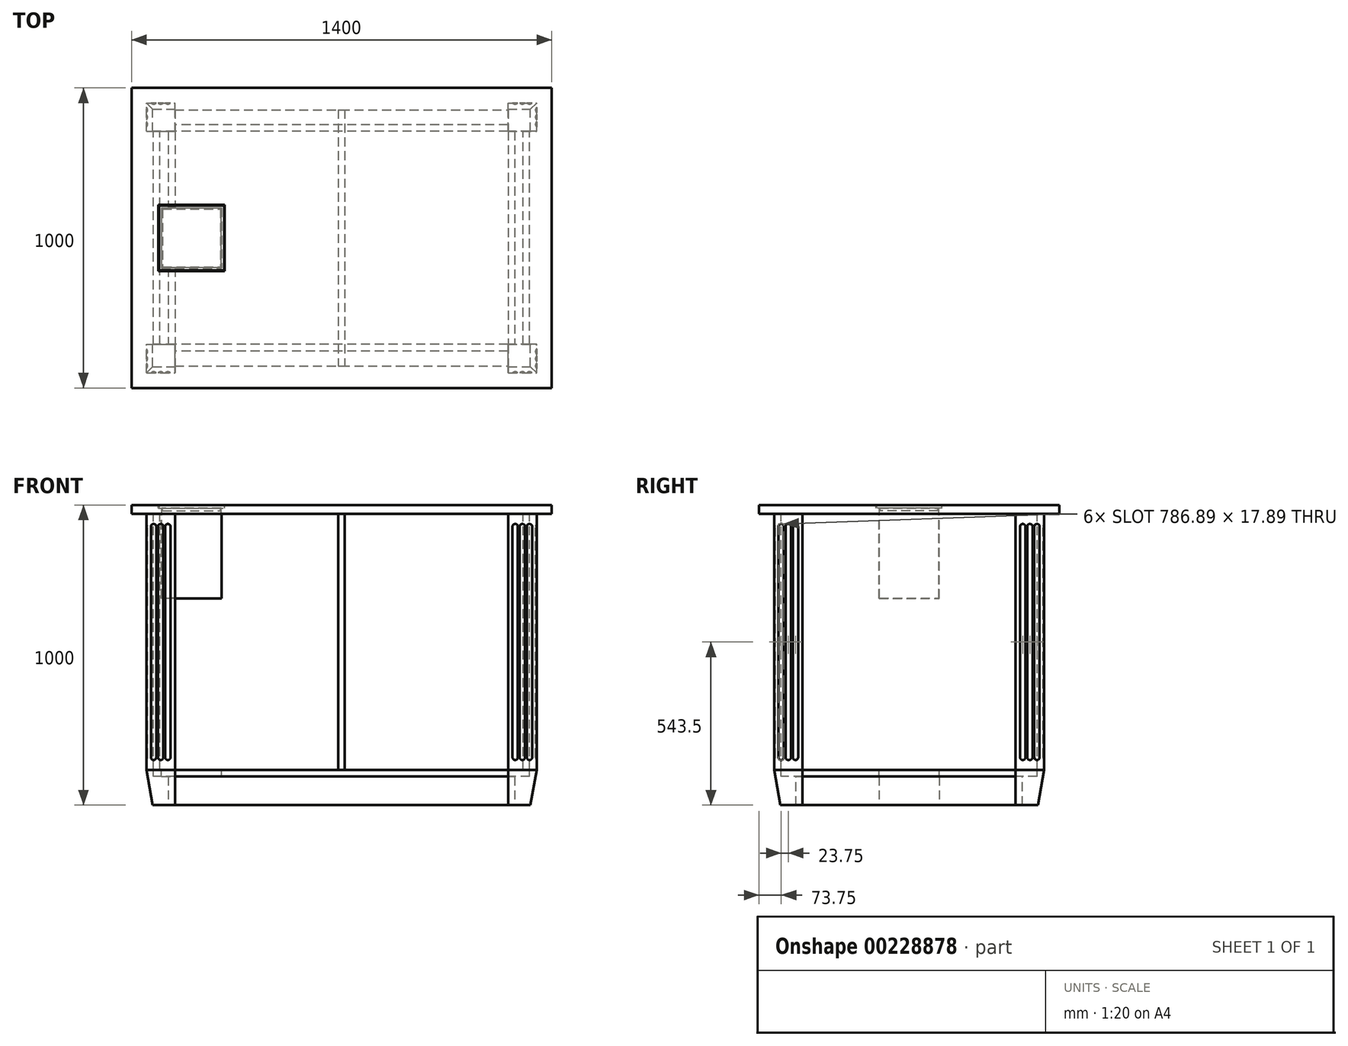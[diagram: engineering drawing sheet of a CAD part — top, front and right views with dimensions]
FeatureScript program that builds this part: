
annotation { "Feature Type Name" : "Feature", "Feature Type Description" : "" }
export const myFeature = defineFeature(function(context is Context, id is Id, definition is map)
    precondition{}
    {
        {
            assignVariable(context, id + "F0", {"name" : "Height", "anyValue" : 1000});
        }
        {
            assignVariable(context, id + "F1", {"name" : "TopThickness", "anyValue" : 30});
        }
        {
            var Q0;
            Q0=qCreatedBy(makeId("Top.planeOp"),FACE);
            cPlane(context, id + "F2", {"entities" : qUnion([Q0]), "cplaneType" : CPlaneType.OFFSET, "offset" : (getVariable(context, 'Height')) * mm, "width" : 150 * mm, "height" : 150 * mm});
        }
        {
            var Q0;
            Q0=qCreatedBy(id+"F2.planeOp",FACE);
            var sketch = newSketch(context, id + "F3", { "sketchPlane" : qUnion([Q0])});
            skLineSegment(sketch, "E0.bottom", {"start": v(700, -500) * mm, "end": v(-700, -500) * mm});
            skLineSegment(sketch, "E0.top", {"start": v(700, 500) * mm, "end": v(-700, 500) * mm});
            skLineSegment(sketch, "E0.left", {"start": v(700, -500) * mm, "end": v(700, 500) * mm});
            skLineSegment(sketch, "E0.right", {"start": v(-700, -500) * mm, "end": v(-700, 500) * mm});
            skPoint(sketch, "E0.middle", {"position": v(0, 0) * mm});
            skSolve(sketch);
        }
        {
            var Q0;
            Q0 = qSketchRegion(id + "F3", true);
            extrude(context, id + "F4", {"entities" : qUnion([Q0]), "oppositeDirection" : true, "depth" : (getVariable(context, 'TopThickness')) * mm});
        }
        {
            var Q0;
            Q0=qCreatedBy(makeId("Top.planeOp"),FACE);
            var sketch = newSketch(context, id + "F5", { "sketchPlane" : qUnion([Q0])});
            skLineSegment(sketch, "E1.bottom", {"start": v(-650, -450) * mm, "end": v(-555, -450) * mm});
            skLineSegment(sketch, "E1.top", {"start": v(-650, -355) * mm, "end": v(-555, -355) * mm});
            skLineSegment(sketch, "E1.left", {"start": v(-650, -450) * mm, "end": v(-650, -355) * mm});
            skLineSegment(sketch, "E1.right", {"start": v(-555, -450) * mm, "end": v(-555, -355) * mm});
            skLineSegment(sketch, "E2.bottom", {"start": v(555, -450) * mm, "end": v(650, -450) * mm});
            skLineSegment(sketch, "E2.top", {"start": v(555, -355) * mm, "end": v(650, -355) * mm});
            skLineSegment(sketch, "E2.left", {"start": v(555, -450) * mm, "end": v(555, -355) * mm});
            skLineSegment(sketch, "E2.right", {"start": v(650, -450) * mm, "end": v(650, -355) * mm});
            skLineSegment(sketch, "E3.bottom", {"start": v(-650, 355) * mm, "end": v(-555, 355) * mm});
            skLineSegment(sketch, "E3.top", {"start": v(-650, 450) * mm, "end": v(-555, 450) * mm});
            skLineSegment(sketch, "E3.left", {"start": v(-650, 355) * mm, "end": v(-650, 450) * mm});
            skLineSegment(sketch, "E3.right", {"start": v(-555, 355) * mm, "end": v(-555, 450) * mm});
            skLineSegment(sketch, "E4.bottom", {"start": v(555, 355) * mm, "end": v(650, 355) * mm});
            skLineSegment(sketch, "E4.top", {"start": v(555, 450) * mm, "end": v(650, 450) * mm});
            skLineSegment(sketch, "E4.left", {"start": v(555, 355) * mm, "end": v(555, 450) * mm});
            skLineSegment(sketch, "E4.right", {"start": v(650, 355) * mm, "end": v(650, 450) * mm});
            skSolve(sketch);
        }
        {
            var Q0;
            Q0 = qSketchRegion(id + "F5", true);
            var Q1;
            Q1=makeQuery(id+"F4.opExtrude","CAP_FACE",FACE,{"disambiguationData":[OSD([sQuery(id+"F3.wireOp",EDGE,"E0.bottom"),sQuery(id+"F3.wireOp",EDGE,"E0.top"),sQuery(id+"F3.wireOp",EDGE,"E0.left"),sQuery(id+"F3.wireOp",EDGE,"E0.right")])],"isStart":false});
            extrude(context, id + "F6", {"entities" : qUnion([Q0]), "endBound" : BoundingType.UP_TO_SURFACE, "endBoundEntityFace" : qUnion([Q1]), "depth" : 25 * mm});
        }
        {
            var Q0;
            Q0=makeQuery(id+"F6.opExtrude","SWEPT_FACE",FACE,{"disambiguationData":[OSD([sQuery(id+"F5.wireOp",EDGE,"E1.right")])]});
            var sketch = newSketch(context, id + "F7", { "sketchPlane" : qUnion([Q0])});
            skLineSegment(sketch, "E5.bottom", {"start": v(-355, 95) * mm, "end": v(-377, 95) * mm});
            skLineSegment(sketch, "E5.top", {"start": v(-355, 0) * mm, "end": v(-377, 0) * mm});
            skLineSegment(sketch, "E5.left", {"start": v(-355, 95) * mm, "end": v(-355, 0) * mm});
            skLineSegment(sketch, "E5.right", {"start": v(-377, 95) * mm, "end": v(-377, 0) * mm});
            skSolve(sketch);
        }
        {
            var Q0;
            Q0 = qSketchRegion(id + "F7", true);
            var Q1;
            Q1=makeQuery(id+"F6.opExtrude","SWEPT_FACE",FACE,{"disambiguationData":[OSD([sQuery(id+"F5.wireOp",EDGE,"E2.left")])]});
            extrude(context, id + "F8", {"entities" : qUnion([Q0]), "endBound" : BoundingType.UP_TO_SURFACE, "endBoundEntityFace" : qUnion([Q1]), "depth" : 25 * mm});
        }
        {
            var Q0;
            Q0=makeQuery(id+"F8.opExtrude","SWEPT_BODY",BODY,{"disambiguationData":[OSD([sQuery(id+"F7.wireOp",EDGE,"E5.bottom"),sQuery(id+"F7.wireOp",EDGE,"E5.top"),sQuery(id+"F7.wireOp",EDGE,"E5.left"),sQuery(id+"F7.wireOp",EDGE,"E5.right")])]});
            var Q1;
            Q1=qCreatedBy(makeId("Front.planeOp"),FACE);
            mirror(context, id + "F9", {"entities" : qUnion([Q0]), "mirrorPlane" : qUnion([Q1])});
        }
        {
            var Q0;
            Q0=makeQuery(id+"F6.opExtrude","SWEPT_FACE",FACE,{"disambiguationData":[OSD([sQuery(id+"F5.wireOp",EDGE,"E2.top")])]});
            var sketch = newSketch(context, id + "F10", { "sketchPlane" : qUnion([Q0])});
            skLineSegment(sketch, "E6.bottom", {"start": v(-555, 95) * mm, "end": v(-577, 95) * mm});
            skLineSegment(sketch, "E6.top", {"start": v(-555, 0) * mm, "end": v(-577, 0) * mm});
            skLineSegment(sketch, "E6.left", {"start": v(-555, 95) * mm, "end": v(-555, 0) * mm});
            skLineSegment(sketch, "E6.right", {"start": v(-577, 95) * mm, "end": v(-577, 0) * mm});
            skSolve(sketch);
        }
        {
            var Q0;
            Q0 = qSketchRegion(id + "F10", true);
            var Q1;
            Q1=makeQuery(id+"F6.opExtrude","SWEPT_FACE",FACE,{"disambiguationData":[OSD([sQuery(id+"F5.wireOp",EDGE,"E4.bottom")])]});
            extrude(context, id + "F11", {"entities" : qUnion([Q0]), "endBound" : BoundingType.UP_TO_SURFACE, "endBoundEntityFace" : qUnion([Q1]), "depth" : 25 * mm});
        }
        {
            var Q0;
            Q0=makeQuery(id+"F11.opExtrude","SWEPT_BODY",BODY,{"disambiguationData":[OSD([sQuery(id+"F10.wireOp",EDGE,"E6.bottom"),sQuery(id+"F10.wireOp",EDGE,"E6.top"),sQuery(id+"F10.wireOp",EDGE,"E6.left"),sQuery(id+"F10.wireOp",EDGE,"E6.right")])]});
            var Q1;
            Q1=qCreatedBy(makeId("Right.planeOp"),FACE);
            mirror(context, id + "F12", {"entities" : qUnion([Q0]), "mirrorPlane" : qUnion([Q1])});
        }
        {
            var Q0;
            Q0=makeQuery(id+"F11.opExtrude","SWEPT_FACE",FACE,{"disambiguationData":[OSD([sQuery(id+"F10.wireOp",EDGE,"E6.bottom")])]});
            var sketch = newSketch(context, id + "F13", { "sketchPlane" : qUnion([Q0])});
            skLineSegment(sketch, "E7.bottom", {"start": v(-627, 427) * mm, "end": v(627, 427) * mm});
            skLineSegment(sketch, "E7.top", {"start": v(-627, -427) * mm, "end": v(627, -427) * mm});
            skLineSegment(sketch, "E7.left", {"start": v(-627, 427) * mm, "end": v(-627, -427) * mm});
            skLineSegment(sketch, "E7.right", {"start": v(627, 427) * mm, "end": v(627, -427) * mm});
            skPoint(sketch, "E7.middle", {"position": v(0, 0) * mm});
            skSolve(sketch);
        }
        {
            var Q0;
            Q0 = qSketchRegion(id + "F13", true);
            extrude(context, id + "F14", {"entities" : qUnion([Q0]), "depth" : 22 * mm});
        }
        {
            var Q0;
            Q0=makeQuery(id+"F6.opExtrude","SWEPT_BODY",BODY,{"disambiguationData":[OSD([sQuery(id+"F5.wireOp",EDGE,"E4.bottom"),sQuery(id+"F5.wireOp",EDGE,"E4.top"),sQuery(id+"F5.wireOp",EDGE,"E4.left"),sQuery(id+"F5.wireOp",EDGE,"E4.right")])]});
            var Q1;
            Q1=makeQuery(id+"F6.opExtrude","SWEPT_BODY",BODY,{"disambiguationData":[OSD([sQuery(id+"F5.wireOp",EDGE,"E2.bottom"),sQuery(id+"F5.wireOp",EDGE,"E2.top"),sQuery(id+"F5.wireOp",EDGE,"E2.left"),sQuery(id+"F5.wireOp",EDGE,"E2.right")])]});
            var Q2;
            Q2=makeQuery(id+"F6.opExtrude","SWEPT_BODY",BODY,{"disambiguationData":[OSD([sQuery(id+"F5.wireOp",EDGE,"E1.bottom"),sQuery(id+"F5.wireOp",EDGE,"E1.top"),sQuery(id+"F5.wireOp",EDGE,"E1.left"),sQuery(id+"F5.wireOp",EDGE,"E1.right")])]});
            var Q3;
            Q3=makeQuery(id+"F6.opExtrude","SWEPT_BODY",BODY,{"disambiguationData":[OSD([sQuery(id+"F5.wireOp",EDGE,"E3.bottom"),sQuery(id+"F5.wireOp",EDGE,"E3.top"),sQuery(id+"F5.wireOp",EDGE,"E3.left"),sQuery(id+"F5.wireOp",EDGE,"E3.right")])]});
            var Q4;
            Q4=makeQuery(id+"F14.opExtrude","SWEPT_BODY",BODY,{"disambiguationData":[OSD([sQuery(id+"F13.wireOp",EDGE,"E7.bottom"),sQuery(id+"F13.wireOp",EDGE,"E7.top"),sQuery(id+"F13.wireOp",EDGE,"E7.left"),sQuery(id+"F13.wireOp",EDGE,"E7.right")])]});
            booleanBodies(context, id + "F15", {"operationType" : BooleanOperationType.SUBTRACTION, "tools" : qUnion([Q0, Q1, Q2, Q3]), "targets" : qUnion([Q4]), "keepTools" : true});
        }
        {
            var Q0;
            Q0=makeQuery(id+"F6.opExtrude","SWEPT_FACE",FACE,{"disambiguationData":[OSD([sQuery(id+"F5.wireOp",EDGE,"E3.bottom")])]});
            var sketch = newSketch(context, id + "F16", { "sketchPlane" : qUnion([Q0])});
            skLineSegment(sketch, "E8.bottom", {"start": v(-627, 970) * mm, "end": v(-605, 970) * mm});
            skLineSegment(sketch, "E8.top", {"start": v(-627, 117) * mm, "end": v(-605, 117) * mm});
            skLineSegment(sketch, "E8.left", {"start": v(-627, 970) * mm, "end": v(-627, 117) * mm});
            skLineSegment(sketch, "E8.right", {"start": v(-605, 970) * mm, "end": v(-605, 117) * mm});
            skSolve(sketch);
        }
        {
            var Q0;
            Q0 = qSketchRegion(id + "F16", true);
            extrude(context, id + "F17", {"entities" : qUnion([Q0]), "endBound" : BoundingType.UP_TO_NEXT, "depth" : 25 * mm});
        }
        {
            var Q0;
            Q0=makeQuery(id+"F17.opExtrude","SWEPT_BODY",BODY,{"disambiguationData":[OSD([sQuery(id+"F16.wireOp",EDGE,"E8.bottom"),sQuery(id+"F16.wireOp",EDGE,"E8.top"),sQuery(id+"F16.wireOp",EDGE,"E8.left"),sQuery(id+"F16.wireOp",EDGE,"E8.right")])]});
            var Q1;
            Q1=qCreatedBy(makeId("Right.planeOp"),FACE);
            mirror(context, id + "F18", {"entities" : qUnion([Q0]), "mirrorPlane" : qUnion([Q1])});
        }
        {
            var Q0;
            Q0=makeQuery(id+"F6.opExtrude","SWEPT_FACE",FACE,{"disambiguationData":[OSD([sQuery(id+"F5.wireOp",EDGE,"E2.right")])]});
            var sketch = newSketch(context, id + "F19", { "sketchPlane" : qUnion([Q0])});
            skLineSegment(sketch, "E9", {"start": v(-450, 117) * mm, "end": v(-424.72, -26.37) * mm});
            skLineSegment(sketch, "E10", {"start": v(-424.72, -26.37) * mm, "end": v(-510.23, -26.37) * mm});
            skLineSegment(sketch, "E11", {"start": v(-510.23, -26.37) * mm, "end": v(-450, 117) * mm});
            skLineSegment(sketch, "E12.0", {"start": v(355, 117) * mm, "end": v(-355, 117) * mm, "construction": true});
            skLineSegment(sketch, "E13", {"start": v(-355, 117) * mm, "end": v(-576.45, 117) * mm, "construction": true});
            skLineSegment(sketch, "E14.0", {"start": v(450, 970) * mm, "end": v(450, 0) * mm, "construction": true});
            skLineSegment(sketch, "E15", {"start": v(355, 117) * mm, "end": v(613.82, 117) * mm, "construction": true});
            skLineSegment(sketch, "E16", {"start": v(450, 117) * mm, "end": v(417.76, -65.85) * mm});
            skLineSegment(sketch, "E17", {"start": v(417.76, -65.85) * mm, "end": v(573.8, -58.45) * mm});
            skLineSegment(sketch, "E18", {"start": v(573.8, -58.45) * mm, "end": v(450, 117) * mm});
            skSolve(sketch);
        }
        {
            var Q0;
            Q0 = qSketchRegion(id + "F19", true);
            extrude(context, id + "F20", {"entities" : qUnion([Q0]), "operationType" : NewBodyOperationType.REMOVE, "endBound" : BoundingType.THROUGH_ALL, "oppositeDirection" : true, "depth" : 25 * mm});
        }
        {
            var Q0;
            Q0=makeQuery(id+"F6.opExtrude","SWEPT_FACE",FACE,{"disambiguationData":[OSD([sQuery(id+"F5.wireOp",EDGE,"E4.top")])]});
            var sketch = newSketch(context, id + "F21", { "sketchPlane" : qUnion([Q0])});
            skLineSegment(sketch, "E19.0", {"start": v(555, 117) * mm, "end": v(-555, 117) * mm, "construction": true});
            skLineSegment(sketch, "E20", {"start": v(-555, 117) * mm, "end": v(-830.8, 117) * mm, "construction": true});
            skLineSegment(sketch, "E21", {"start": v(-650, 117) * mm, "end": v(-621.11, -46.82) * mm});
            skLineSegment(sketch, "E22", {"start": v(-621.11, -46.82) * mm, "end": v(-744.4, -46.82) * mm});
            skLineSegment(sketch, "E23", {"start": v(-744.4, -46.82) * mm, "end": v(-650, 117) * mm});
            skLineSegment(sketch, "E24", {"start": v(650, 117) * mm, "end": v(608.3, -119.45) * mm});
            skLineSegment(sketch, "E25", {"start": v(608.3, -119.45) * mm, "end": v(784.77, -119.45) * mm});
            skLineSegment(sketch, "E26", {"start": v(784.77, -119.45) * mm, "end": v(650, 117) * mm});
            skLineSegment(sketch, "E27.0", {"start": v(650, 970) * mm, "end": v(650, 0) * mm, "construction": true});
            skLineSegment(sketch, "E28", {"start": v(555, 117) * mm, "end": v(857.57, 117) * mm, "construction": true});
            skSolve(sketch);
        }
        {
            var Q0;
            Q0 = qSketchRegion(id + "F21", true);
            extrude(context, id + "F22", {"entities" : qUnion([Q0]), "operationType" : NewBodyOperationType.REMOVE, "endBound" : BoundingType.THROUGH_ALL, "oppositeDirection" : true, "depth" : 25 * mm});
        }
        {
            var Q0;
            Q0=makeQuery(id+"F6.opExtrude","SWEPT_FACE",FACE,{"disambiguationData":[OSD([sQuery(id+"F5.wireOp",EDGE,"E2.top")])]});
            var Q1;
            Q1=makeQuery(id+"F6.opExtrude","SWEPT_FACE",FACE,{"disambiguationData":[OSD([sQuery(id+"F5.wireOp",EDGE,"E2.bottom")])]});
            cPlane(context, id + "F23", {"entities" : qUnion([Q0, Q1]), "cplaneType" : CPlaneType.MID_PLANE, "offset" : 25 * mm, "width" : 150 * mm, "height" : 150 * mm});
        }
        {
            var Q0;
            Q0=qCreatedBy(id+"F23.planeOp",FACE);
            var sketch = newSketch(context, id + "F24", { "sketchPlane" : qUnion([Q0])});
            skLineSegment(sketch, "E29", {"start": v(-658, 940) * mm, "end": v(-658, 147) * mm});
            skLineSegment(sketch, "E30", {"start": v(-646, 928) * mm, "end": v(-646, 159) * mm});
            skLineSegment(sketch, "E31.0", {"start": v(-555, 117) * mm, "end": v(-650, 117) * mm, "construction": true});
            skLineSegment(sketch, "E32.0", {"start": v(-700, 970) * mm, "end": v(700, 970) * mm, "construction": true});
            skArc(sketch, "E33", {"start": v(-646, 159) * mm, "mid": v(-649.51, 150.51) * mm, "end": v(-658, 147) * mm});
            skArc(sketch, "E34", {"start": v(-646, 928) * mm, "mid": v(-649.51, 936.49) * mm, "end": v(-658, 940) * mm});
            skSolve(sketch);
        }
        {
            var Q0;
            Q0 = qSketchRegion(id + "F24", true);
            var Q1;
            Q1=sQuery(id+"F24.wireOp",EDGE,"E29");
            revolve(context, id + "F25", {"entities" : qUnion([Q0]), "axis" : qUnion([Q1]), "revolveType" : RevolveType.FULL});
        }
        {
            var Q0;
            Q0=makeQuery(id+"F25.opRevolve","SWEPT_BODY",BODY,{"disambiguationData":[OSD([sQuery(id+"F24.wireOp",EDGE,"E29"),sQuery(id+"F24.wireOp",EDGE,"E30"),sQuery(id+"F24.wireOp",EDGE,"E33"),sQuery(id+"F24.wireOp",EDGE,"E34")])]});
            var Q1;
            Q1=makeQuery(id+"F6.opExtrude","CAP_EDGE",EDGE,{"disambiguationData":[OSD([sQuery(id+"F5.wireOp",EDGE,"E2.right")])],"isStart":false});
            transform(context, id + "F26", {"entities" : qUnion([Q0]), "transformType" : TransformType.TRANSLATION_DISTANCE, "transformDirection" : qUnion([Q1]), "distance" : (95 / 4) * mm, "makeCopy" : true});
        }
        {
            var Q0;
            Q0=makeQuery(id+"F25.opRevolve","SWEPT_BODY",BODY,{"disambiguationData":[OSD([sQuery(id+"F24.wireOp",EDGE,"E29"),sQuery(id+"F24.wireOp",EDGE,"E30"),sQuery(id+"F24.wireOp",EDGE,"E33"),sQuery(id+"F24.wireOp",EDGE,"E34")])]});
            var Q1;
            Q1=makeQuery(id+"F6.opExtrude","CAP_EDGE",EDGE,{"disambiguationData":[OSD([sQuery(id+"F5.wireOp",EDGE,"E2.right")])],"isStart":false});
            transform(context, id + "F27", {"entities" : qUnion([Q0]), "transformType" : TransformType.TRANSLATION_DISTANCE, "transformDirection" : qUnion([Q1]), "distance" : (95 / 4) * mm, "oppositeDirection" : true, "makeCopy" : true});
        }
        {
            var Q0;
            Q0=makeQuery(id+"F27.opPattern","COPY",BODY,{"derivedFrom":makeQuery(id+"F25.opRevolve","SWEPT_BODY",BODY,{"disambiguationData":[OSD([sQuery(id+"F24.wireOp",EDGE,"E29"),sQuery(id+"F24.wireOp",EDGE,"E30"),sQuery(id+"F24.wireOp",EDGE,"E33"),sQuery(id+"F24.wireOp",EDGE,"E34")])]}),"instanceName":"1"});
            var Q1;
            Q1=makeQuery(id+"F25.opRevolve","SWEPT_BODY",BODY,{"disambiguationData":[OSD([sQuery(id+"F24.wireOp",EDGE,"E29"),sQuery(id+"F24.wireOp",EDGE,"E30"),sQuery(id+"F24.wireOp",EDGE,"E33"),sQuery(id+"F24.wireOp",EDGE,"E34")])]});
            var Q2;
            Q2=makeQuery(id+"F26.opPattern","COPY",BODY,{"derivedFrom":makeQuery(id+"F25.opRevolve","SWEPT_BODY",BODY,{"disambiguationData":[OSD([sQuery(id+"F24.wireOp",EDGE,"E29"),sQuery(id+"F24.wireOp",EDGE,"E30"),sQuery(id+"F24.wireOp",EDGE,"E33"),sQuery(id+"F24.wireOp",EDGE,"E34")])]}),"instanceName":"1"});
            var Q3;
            Q3=qCreatedBy(makeId("Front.planeOp"),FACE);
            mirror(context, id + "F28", {"entities" : qUnion([Q0, Q1, Q2]), "mirrorPlane" : qUnion([Q3])});
        }
        {
            var Q0;
            Q0=makeQuery(id+"F27.opPattern","COPY",BODY,{"derivedFrom":makeQuery(id+"F25.opRevolve","SWEPT_BODY",BODY,{"disambiguationData":[OSD([sQuery(id+"F24.wireOp",EDGE,"E29"),sQuery(id+"F24.wireOp",EDGE,"E30"),sQuery(id+"F24.wireOp",EDGE,"E33"),sQuery(id+"F24.wireOp",EDGE,"E34")])]}),"instanceName":"1"});
            var Q1;
            Q1=makeQuery(id+"F25.opRevolve","SWEPT_BODY",BODY,{"disambiguationData":[OSD([sQuery(id+"F24.wireOp",EDGE,"E29"),sQuery(id+"F24.wireOp",EDGE,"E30"),sQuery(id+"F24.wireOp",EDGE,"E33"),sQuery(id+"F24.wireOp",EDGE,"E34")])]});
            var Q2;
            Q2=makeQuery(id+"F26.opPattern","COPY",BODY,{"derivedFrom":makeQuery(id+"F25.opRevolve","SWEPT_BODY",BODY,{"disambiguationData":[OSD([sQuery(id+"F24.wireOp",EDGE,"E29"),sQuery(id+"F24.wireOp",EDGE,"E30"),sQuery(id+"F24.wireOp",EDGE,"E33"),sQuery(id+"F24.wireOp",EDGE,"E34")])]}),"instanceName":"1"});
            var Q3;
            Q3=makeQuery(id+"F28.opPattern","COPY",BODY,{"derivedFrom":makeQuery(id+"F26.opPattern","COPY",BODY,{"derivedFrom":makeQuery(id+"F25.opRevolve","SWEPT_BODY",BODY,{"disambiguationData":[OSD([sQuery(id+"F24.wireOp",EDGE,"E29"),sQuery(id+"F24.wireOp",EDGE,"E30"),sQuery(id+"F24.wireOp",EDGE,"E33"),sQuery(id+"F24.wireOp",EDGE,"E34")])]}),"instanceName":"1"}),"instanceName":"1"});
            var Q4;
            Q4=makeQuery(id+"F28.opPattern","COPY",BODY,{"derivedFrom":makeQuery(id+"F25.opRevolve","SWEPT_BODY",BODY,{"disambiguationData":[OSD([sQuery(id+"F24.wireOp",EDGE,"E29"),sQuery(id+"F24.wireOp",EDGE,"E30"),sQuery(id+"F24.wireOp",EDGE,"E33"),sQuery(id+"F24.wireOp",EDGE,"E34")])]}),"instanceName":"1"});
            var Q5;
            Q5=makeQuery(id+"F28.opPattern","COPY",BODY,{"derivedFrom":makeQuery(id+"F27.opPattern","COPY",BODY,{"derivedFrom":makeQuery(id+"F25.opRevolve","SWEPT_BODY",BODY,{"disambiguationData":[OSD([sQuery(id+"F24.wireOp",EDGE,"E29"),sQuery(id+"F24.wireOp",EDGE,"E30"),sQuery(id+"F24.wireOp",EDGE,"E33"),sQuery(id+"F24.wireOp",EDGE,"E34")])]}),"instanceName":"1"}),"instanceName":"1"});
            var Q6;
            Q6=qCreatedBy(makeId("Right.planeOp"),FACE);
            mirror(context, id + "F29", {"entities" : qUnion([Q0, Q1, Q2, Q3, Q4, Q5]), "mirrorPlane" : qUnion([Q6])});
        }
        {
            var Q0;
            Q0=qCreatedBy(id+"F23.planeOp",FACE);
            var sketch = newSketch(context, id + "F30", { "sketchPlane" : qUnion([Q0])});
            skLineSegment(sketch, "E35", {"start": v(-602.5, 1052.6) * mm, "end": v(-602.5, -128.46) * mm, "construction": true});
            skSolve(sketch);
        }
        {
            var Q0;
            Q0=makeQuery(id+"F27.opPattern","COPY",BODY,{"derivedFrom":makeQuery(id+"F25.opRevolve","SWEPT_BODY",BODY,{"disambiguationData":[OSD([sQuery(id+"F24.wireOp",EDGE,"E29"),sQuery(id+"F24.wireOp",EDGE,"E30"),sQuery(id+"F24.wireOp",EDGE,"E33"),sQuery(id+"F24.wireOp",EDGE,"E34")])]}),"instanceName":"1"});
            var Q1;
            Q1=makeQuery(id+"F25.opRevolve","SWEPT_BODY",BODY,{"disambiguationData":[OSD([sQuery(id+"F24.wireOp",EDGE,"E29"),sQuery(id+"F24.wireOp",EDGE,"E30"),sQuery(id+"F24.wireOp",EDGE,"E33"),sQuery(id+"F24.wireOp",EDGE,"E34")])]});
            var Q2;
            Q2=makeQuery(id+"F26.opPattern","COPY",BODY,{"derivedFrom":makeQuery(id+"F25.opRevolve","SWEPT_BODY",BODY,{"disambiguationData":[OSD([sQuery(id+"F24.wireOp",EDGE,"E29"),sQuery(id+"F24.wireOp",EDGE,"E30"),sQuery(id+"F24.wireOp",EDGE,"E33"),sQuery(id+"F24.wireOp",EDGE,"E34")])]}),"instanceName":"1"});
            var Q3;
            Q3=sQuery(id+"F30.wireOp",EDGE,"E35");
            transform(context, id + "F31", {"entities" : qUnion([Q0, Q1, Q2]), "transformType" : TransformType.ROTATION, "transformAxis" : qUnion([Q3]), "angle" : 90 * degree, "makeCopy" : true});
        }
        {
            var Q0;
            Q0=makeQuery(id+"F31.opPattern","COPY",BODY,{"derivedFrom":makeQuery(id+"F27.opPattern","COPY",BODY,{"derivedFrom":makeQuery(id+"F25.opRevolve","SWEPT_BODY",BODY,{"disambiguationData":[OSD([sQuery(id+"F24.wireOp",EDGE,"E29"),sQuery(id+"F24.wireOp",EDGE,"E30"),sQuery(id+"F24.wireOp",EDGE,"E33"),sQuery(id+"F24.wireOp",EDGE,"E34")])]}),"instanceName":"1"}),"instanceName":"1"});
            var Q1;
            Q1=makeQuery(id+"F31.opPattern","COPY",BODY,{"derivedFrom":makeQuery(id+"F25.opRevolve","SWEPT_BODY",BODY,{"disambiguationData":[OSD([sQuery(id+"F24.wireOp",EDGE,"E29"),sQuery(id+"F24.wireOp",EDGE,"E30"),sQuery(id+"F24.wireOp",EDGE,"E33"),sQuery(id+"F24.wireOp",EDGE,"E34")])]}),"instanceName":"1"});
            var Q2;
            Q2=makeQuery(id+"F31.opPattern","COPY",BODY,{"derivedFrom":makeQuery(id+"F26.opPattern","COPY",BODY,{"derivedFrom":makeQuery(id+"F25.opRevolve","SWEPT_BODY",BODY,{"disambiguationData":[OSD([sQuery(id+"F24.wireOp",EDGE,"E29"),sQuery(id+"F24.wireOp",EDGE,"E30"),sQuery(id+"F24.wireOp",EDGE,"E33"),sQuery(id+"F24.wireOp",EDGE,"E34")])]}),"instanceName":"1"}),"instanceName":"1"});
            var Q3;
            Q3=qCreatedBy(makeId("Right.planeOp"),FACE);
            mirror(context, id + "F32", {"entities" : qUnion([Q0, Q1, Q2]), "mirrorPlane" : qUnion([Q3])});
        }
        {
            var Q0;
            Q0=makeQuery(id+"F32.opPattern","COPY",BODY,{"derivedFrom":makeQuery(id+"F31.opPattern","COPY",BODY,{"derivedFrom":makeQuery(id+"F26.opPattern","COPY",BODY,{"derivedFrom":makeQuery(id+"F25.opRevolve","SWEPT_BODY",BODY,{"disambiguationData":[OSD([sQuery(id+"F24.wireOp",EDGE,"E29"),sQuery(id+"F24.wireOp",EDGE,"E30"),sQuery(id+"F24.wireOp",EDGE,"E33"),sQuery(id+"F24.wireOp",EDGE,"E34")])]}),"instanceName":"1"}),"instanceName":"1"}),"instanceName":"1"});
            var Q1;
            Q1=makeQuery(id+"F32.opPattern","COPY",BODY,{"derivedFrom":makeQuery(id+"F31.opPattern","COPY",BODY,{"derivedFrom":makeQuery(id+"F25.opRevolve","SWEPT_BODY",BODY,{"disambiguationData":[OSD([sQuery(id+"F24.wireOp",EDGE,"E29"),sQuery(id+"F24.wireOp",EDGE,"E30"),sQuery(id+"F24.wireOp",EDGE,"E33"),sQuery(id+"F24.wireOp",EDGE,"E34")])]}),"instanceName":"1"}),"instanceName":"1"});
            var Q2;
            Q2=makeQuery(id+"F32.opPattern","COPY",BODY,{"derivedFrom":makeQuery(id+"F31.opPattern","COPY",BODY,{"derivedFrom":makeQuery(id+"F27.opPattern","COPY",BODY,{"derivedFrom":makeQuery(id+"F25.opRevolve","SWEPT_BODY",BODY,{"disambiguationData":[OSD([sQuery(id+"F24.wireOp",EDGE,"E29"),sQuery(id+"F24.wireOp",EDGE,"E30"),sQuery(id+"F24.wireOp",EDGE,"E33"),sQuery(id+"F24.wireOp",EDGE,"E34")])]}),"instanceName":"1"}),"instanceName":"1"}),"instanceName":"1"});
            var Q3;
            Q3=makeQuery(id+"F31.opPattern","COPY",BODY,{"derivedFrom":makeQuery(id+"F27.opPattern","COPY",BODY,{"derivedFrom":makeQuery(id+"F25.opRevolve","SWEPT_BODY",BODY,{"disambiguationData":[OSD([sQuery(id+"F24.wireOp",EDGE,"E29"),sQuery(id+"F24.wireOp",EDGE,"E30"),sQuery(id+"F24.wireOp",EDGE,"E33"),sQuery(id+"F24.wireOp",EDGE,"E34")])]}),"instanceName":"1"}),"instanceName":"1"});
            var Q4;
            Q4=makeQuery(id+"F31.opPattern","COPY",BODY,{"derivedFrom":makeQuery(id+"F25.opRevolve","SWEPT_BODY",BODY,{"disambiguationData":[OSD([sQuery(id+"F24.wireOp",EDGE,"E29"),sQuery(id+"F24.wireOp",EDGE,"E30"),sQuery(id+"F24.wireOp",EDGE,"E33"),sQuery(id+"F24.wireOp",EDGE,"E34")])]}),"instanceName":"1"});
            var Q5;
            Q5=makeQuery(id+"F31.opPattern","COPY",BODY,{"derivedFrom":makeQuery(id+"F26.opPattern","COPY",BODY,{"derivedFrom":makeQuery(id+"F25.opRevolve","SWEPT_BODY",BODY,{"disambiguationData":[OSD([sQuery(id+"F24.wireOp",EDGE,"E29"),sQuery(id+"F24.wireOp",EDGE,"E30"),sQuery(id+"F24.wireOp",EDGE,"E33"),sQuery(id+"F24.wireOp",EDGE,"E34")])]}),"instanceName":"1"}),"instanceName":"1"});
            var Q6;
            Q6=qCreatedBy(makeId("Front.planeOp"),FACE);
            mirror(context, id + "F33", {"entities" : qUnion([Q0, Q1, Q2, Q3, Q4, Q5]), "mirrorPlane" : qUnion([Q6])});
        }
        {
            var Q0;
            Q0=makeQuery(id+"F32.opPattern","COPY",BODY,{"derivedFrom":makeQuery(id+"F31.opPattern","COPY",BODY,{"derivedFrom":makeQuery(id+"F26.opPattern","COPY",BODY,{"derivedFrom":makeQuery(id+"F25.opRevolve","SWEPT_BODY",BODY,{"disambiguationData":[OSD([sQuery(id+"F24.wireOp",EDGE,"E29"),sQuery(id+"F24.wireOp",EDGE,"E30"),sQuery(id+"F24.wireOp",EDGE,"E33"),sQuery(id+"F24.wireOp",EDGE,"E34")])]}),"instanceName":"1"}),"instanceName":"1"}),"instanceName":"1"});
            var Q1;
            Q1=makeQuery(id+"F32.opPattern","COPY",BODY,{"derivedFrom":makeQuery(id+"F31.opPattern","COPY",BODY,{"derivedFrom":makeQuery(id+"F25.opRevolve","SWEPT_BODY",BODY,{"disambiguationData":[OSD([sQuery(id+"F24.wireOp",EDGE,"E29"),sQuery(id+"F24.wireOp",EDGE,"E30"),sQuery(id+"F24.wireOp",EDGE,"E33"),sQuery(id+"F24.wireOp",EDGE,"E34")])]}),"instanceName":"1"}),"instanceName":"1"});
            var Q2;
            Q2=makeQuery(id+"F32.opPattern","COPY",BODY,{"derivedFrom":makeQuery(id+"F31.opPattern","COPY",BODY,{"derivedFrom":makeQuery(id+"F27.opPattern","COPY",BODY,{"derivedFrom":makeQuery(id+"F25.opRevolve","SWEPT_BODY",BODY,{"disambiguationData":[OSD([sQuery(id+"F24.wireOp",EDGE,"E29"),sQuery(id+"F24.wireOp",EDGE,"E30"),sQuery(id+"F24.wireOp",EDGE,"E33"),sQuery(id+"F24.wireOp",EDGE,"E34")])]}),"instanceName":"1"}),"instanceName":"1"}),"instanceName":"1"});
            var Q3;
            Q3=makeQuery(id+"F29.opPattern","COPY",BODY,{"derivedFrom":makeQuery(id+"F26.opPattern","COPY",BODY,{"derivedFrom":makeQuery(id+"F25.opRevolve","SWEPT_BODY",BODY,{"disambiguationData":[OSD([sQuery(id+"F24.wireOp",EDGE,"E29"),sQuery(id+"F24.wireOp",EDGE,"E30"),sQuery(id+"F24.wireOp",EDGE,"E33"),sQuery(id+"F24.wireOp",EDGE,"E34")])]}),"instanceName":"1"}),"instanceName":"1"});
            var Q4;
            Q4=makeQuery(id+"F29.opPattern","COPY",BODY,{"derivedFrom":makeQuery(id+"F25.opRevolve","SWEPT_BODY",BODY,{"disambiguationData":[OSD([sQuery(id+"F24.wireOp",EDGE,"E29"),sQuery(id+"F24.wireOp",EDGE,"E30"),sQuery(id+"F24.wireOp",EDGE,"E33"),sQuery(id+"F24.wireOp",EDGE,"E34")])]}),"instanceName":"1"});
            var Q5;
            Q5=makeQuery(id+"F29.opPattern","COPY",BODY,{"derivedFrom":makeQuery(id+"F27.opPattern","COPY",BODY,{"derivedFrom":makeQuery(id+"F25.opRevolve","SWEPT_BODY",BODY,{"disambiguationData":[OSD([sQuery(id+"F24.wireOp",EDGE,"E29"),sQuery(id+"F24.wireOp",EDGE,"E30"),sQuery(id+"F24.wireOp",EDGE,"E33"),sQuery(id+"F24.wireOp",EDGE,"E34")])]}),"instanceName":"1"}),"instanceName":"1"});
            var Q6;
            Q6=makeQuery(id+"F29.opPattern","COPY",BODY,{"derivedFrom":makeQuery(id+"F28.opPattern","COPY",BODY,{"derivedFrom":makeQuery(id+"F27.opPattern","COPY",BODY,{"derivedFrom":makeQuery(id+"F25.opRevolve","SWEPT_BODY",BODY,{"disambiguationData":[OSD([sQuery(id+"F24.wireOp",EDGE,"E29"),sQuery(id+"F24.wireOp",EDGE,"E30"),sQuery(id+"F24.wireOp",EDGE,"E33"),sQuery(id+"F24.wireOp",EDGE,"E34")])]}),"instanceName":"1"}),"instanceName":"1"}),"instanceName":"1"});
            var Q7;
            Q7=makeQuery(id+"F29.opPattern","COPY",BODY,{"derivedFrom":makeQuery(id+"F28.opPattern","COPY",BODY,{"derivedFrom":makeQuery(id+"F25.opRevolve","SWEPT_BODY",BODY,{"disambiguationData":[OSD([sQuery(id+"F24.wireOp",EDGE,"E29"),sQuery(id+"F24.wireOp",EDGE,"E30"),sQuery(id+"F24.wireOp",EDGE,"E33"),sQuery(id+"F24.wireOp",EDGE,"E34")])]}),"instanceName":"1"}),"instanceName":"1"});
            var Q8;
            Q8=makeQuery(id+"F29.opPattern","COPY",BODY,{"derivedFrom":makeQuery(id+"F28.opPattern","COPY",BODY,{"derivedFrom":makeQuery(id+"F26.opPattern","COPY",BODY,{"derivedFrom":makeQuery(id+"F25.opRevolve","SWEPT_BODY",BODY,{"disambiguationData":[OSD([sQuery(id+"F24.wireOp",EDGE,"E29"),sQuery(id+"F24.wireOp",EDGE,"E30"),sQuery(id+"F24.wireOp",EDGE,"E33"),sQuery(id+"F24.wireOp",EDGE,"E34")])]}),"instanceName":"1"}),"instanceName":"1"}),"instanceName":"1"});
            var Q9;
            Q9=makeQuery(id+"F33.opPattern","COPY",BODY,{"derivedFrom":makeQuery(id+"F32.opPattern","COPY",BODY,{"derivedFrom":makeQuery(id+"F31.opPattern","COPY",BODY,{"derivedFrom":makeQuery(id+"F27.opPattern","COPY",BODY,{"derivedFrom":makeQuery(id+"F25.opRevolve","SWEPT_BODY",BODY,{"disambiguationData":[OSD([sQuery(id+"F24.wireOp",EDGE,"E29"),sQuery(id+"F24.wireOp",EDGE,"E30"),sQuery(id+"F24.wireOp",EDGE,"E33"),sQuery(id+"F24.wireOp",EDGE,"E34")])]}),"instanceName":"1"}),"instanceName":"1"}),"instanceName":"1"}),"instanceName":"1"});
            var Q10;
            Q10=makeQuery(id+"F33.opPattern","COPY",BODY,{"derivedFrom":makeQuery(id+"F32.opPattern","COPY",BODY,{"derivedFrom":makeQuery(id+"F31.opPattern","COPY",BODY,{"derivedFrom":makeQuery(id+"F25.opRevolve","SWEPT_BODY",BODY,{"disambiguationData":[OSD([sQuery(id+"F24.wireOp",EDGE,"E29"),sQuery(id+"F24.wireOp",EDGE,"E30"),sQuery(id+"F24.wireOp",EDGE,"E33"),sQuery(id+"F24.wireOp",EDGE,"E34")])]}),"instanceName":"1"}),"instanceName":"1"}),"instanceName":"1"});
            var Q11;
            Q11=makeQuery(id+"F33.opPattern","COPY",BODY,{"derivedFrom":makeQuery(id+"F32.opPattern","COPY",BODY,{"derivedFrom":makeQuery(id+"F31.opPattern","COPY",BODY,{"derivedFrom":makeQuery(id+"F26.opPattern","COPY",BODY,{"derivedFrom":makeQuery(id+"F25.opRevolve","SWEPT_BODY",BODY,{"disambiguationData":[OSD([sQuery(id+"F24.wireOp",EDGE,"E29"),sQuery(id+"F24.wireOp",EDGE,"E30"),sQuery(id+"F24.wireOp",EDGE,"E33"),sQuery(id+"F24.wireOp",EDGE,"E34")])]}),"instanceName":"1"}),"instanceName":"1"}),"instanceName":"1"}),"instanceName":"1"});
            var Q12;
            Q12=makeQuery(id+"F33.opPattern","COPY",BODY,{"derivedFrom":makeQuery(id+"F31.opPattern","COPY",BODY,{"derivedFrom":makeQuery(id+"F26.opPattern","COPY",BODY,{"derivedFrom":makeQuery(id+"F25.opRevolve","SWEPT_BODY",BODY,{"disambiguationData":[OSD([sQuery(id+"F24.wireOp",EDGE,"E29"),sQuery(id+"F24.wireOp",EDGE,"E30"),sQuery(id+"F24.wireOp",EDGE,"E33"),sQuery(id+"F24.wireOp",EDGE,"E34")])]}),"instanceName":"1"}),"instanceName":"1"}),"instanceName":"1"});
            var Q13;
            Q13=makeQuery(id+"F33.opPattern","COPY",BODY,{"derivedFrom":makeQuery(id+"F31.opPattern","COPY",BODY,{"derivedFrom":makeQuery(id+"F25.opRevolve","SWEPT_BODY",BODY,{"disambiguationData":[OSD([sQuery(id+"F24.wireOp",EDGE,"E29"),sQuery(id+"F24.wireOp",EDGE,"E30"),sQuery(id+"F24.wireOp",EDGE,"E33"),sQuery(id+"F24.wireOp",EDGE,"E34")])]}),"instanceName":"1"}),"instanceName":"1"});
            var Q14;
            Q14=makeQuery(id+"F33.opPattern","COPY",BODY,{"derivedFrom":makeQuery(id+"F31.opPattern","COPY",BODY,{"derivedFrom":makeQuery(id+"F27.opPattern","COPY",BODY,{"derivedFrom":makeQuery(id+"F25.opRevolve","SWEPT_BODY",BODY,{"disambiguationData":[OSD([sQuery(id+"F24.wireOp",EDGE,"E29"),sQuery(id+"F24.wireOp",EDGE,"E30"),sQuery(id+"F24.wireOp",EDGE,"E33"),sQuery(id+"F24.wireOp",EDGE,"E34")])]}),"instanceName":"1"}),"instanceName":"1"}),"instanceName":"1"});
            var Q15;
            Q15=makeQuery(id+"F28.opPattern","COPY",BODY,{"derivedFrom":makeQuery(id+"F26.opPattern","COPY",BODY,{"derivedFrom":makeQuery(id+"F25.opRevolve","SWEPT_BODY",BODY,{"disambiguationData":[OSD([sQuery(id+"F24.wireOp",EDGE,"E29"),sQuery(id+"F24.wireOp",EDGE,"E30"),sQuery(id+"F24.wireOp",EDGE,"E33"),sQuery(id+"F24.wireOp",EDGE,"E34")])]}),"instanceName":"1"}),"instanceName":"1"});
            var Q16;
            Q16=makeQuery(id+"F28.opPattern","COPY",BODY,{"derivedFrom":makeQuery(id+"F25.opRevolve","SWEPT_BODY",BODY,{"disambiguationData":[OSD([sQuery(id+"F24.wireOp",EDGE,"E29"),sQuery(id+"F24.wireOp",EDGE,"E30"),sQuery(id+"F24.wireOp",EDGE,"E33"),sQuery(id+"F24.wireOp",EDGE,"E34")])]}),"instanceName":"1"});
            var Q17;
            Q17=makeQuery(id+"F28.opPattern","COPY",BODY,{"derivedFrom":makeQuery(id+"F27.opPattern","COPY",BODY,{"derivedFrom":makeQuery(id+"F25.opRevolve","SWEPT_BODY",BODY,{"disambiguationData":[OSD([sQuery(id+"F24.wireOp",EDGE,"E29"),sQuery(id+"F24.wireOp",EDGE,"E30"),sQuery(id+"F24.wireOp",EDGE,"E33"),sQuery(id+"F24.wireOp",EDGE,"E34")])]}),"instanceName":"1"}),"instanceName":"1"});
            var Q18;
            Q18=makeQuery(id+"F27.opPattern","COPY",BODY,{"derivedFrom":makeQuery(id+"F25.opRevolve","SWEPT_BODY",BODY,{"disambiguationData":[OSD([sQuery(id+"F24.wireOp",EDGE,"E29"),sQuery(id+"F24.wireOp",EDGE,"E30"),sQuery(id+"F24.wireOp",EDGE,"E33"),sQuery(id+"F24.wireOp",EDGE,"E34")])]}),"instanceName":"1"});
            var Q19;
            Q19=makeQuery(id+"F25.opRevolve","SWEPT_BODY",BODY,{"disambiguationData":[OSD([sQuery(id+"F24.wireOp",EDGE,"E29"),sQuery(id+"F24.wireOp",EDGE,"E30"),sQuery(id+"F24.wireOp",EDGE,"E33"),sQuery(id+"F24.wireOp",EDGE,"E34")])]});
            var Q20;
            Q20=makeQuery(id+"F26.opPattern","COPY",BODY,{"derivedFrom":makeQuery(id+"F25.opRevolve","SWEPT_BODY",BODY,{"disambiguationData":[OSD([sQuery(id+"F24.wireOp",EDGE,"E29"),sQuery(id+"F24.wireOp",EDGE,"E30"),sQuery(id+"F24.wireOp",EDGE,"E33"),sQuery(id+"F24.wireOp",EDGE,"E34")])]}),"instanceName":"1"});
            var Q21;
            Q21=makeQuery(id+"F31.opPattern","COPY",BODY,{"derivedFrom":makeQuery(id+"F27.opPattern","COPY",BODY,{"derivedFrom":makeQuery(id+"F25.opRevolve","SWEPT_BODY",BODY,{"disambiguationData":[OSD([sQuery(id+"F24.wireOp",EDGE,"E29"),sQuery(id+"F24.wireOp",EDGE,"E30"),sQuery(id+"F24.wireOp",EDGE,"E33"),sQuery(id+"F24.wireOp",EDGE,"E34")])]}),"instanceName":"1"}),"instanceName":"1"});
            var Q22;
            Q22=makeQuery(id+"F31.opPattern","COPY",BODY,{"derivedFrom":makeQuery(id+"F25.opRevolve","SWEPT_BODY",BODY,{"disambiguationData":[OSD([sQuery(id+"F24.wireOp",EDGE,"E29"),sQuery(id+"F24.wireOp",EDGE,"E30"),sQuery(id+"F24.wireOp",EDGE,"E33"),sQuery(id+"F24.wireOp",EDGE,"E34")])]}),"instanceName":"1"});
            var Q23;
            Q23=makeQuery(id+"F31.opPattern","COPY",BODY,{"derivedFrom":makeQuery(id+"F26.opPattern","COPY",BODY,{"derivedFrom":makeQuery(id+"F25.opRevolve","SWEPT_BODY",BODY,{"disambiguationData":[OSD([sQuery(id+"F24.wireOp",EDGE,"E29"),sQuery(id+"F24.wireOp",EDGE,"E30"),sQuery(id+"F24.wireOp",EDGE,"E33"),sQuery(id+"F24.wireOp",EDGE,"E34")])]}),"instanceName":"1"}),"instanceName":"1"});
            var Q24;
            Q24=makeQuery(id+"F6.opExtrude","SWEPT_BODY",BODY,{"disambiguationData":[OSD([sQuery(id+"F5.wireOp",EDGE,"E2.bottom"),sQuery(id+"F5.wireOp",EDGE,"E2.top"),sQuery(id+"F5.wireOp",EDGE,"E2.left"),sQuery(id+"F5.wireOp",EDGE,"E2.right")])]});
            var Q25;
            Q25=makeQuery(id+"F6.opExtrude","SWEPT_BODY",BODY,{"disambiguationData":[OSD([sQuery(id+"F5.wireOp",EDGE,"E4.bottom"),sQuery(id+"F5.wireOp",EDGE,"E4.top"),sQuery(id+"F5.wireOp",EDGE,"E4.left"),sQuery(id+"F5.wireOp",EDGE,"E4.right")])]});
            var Q26;
            Q26=makeQuery(id+"F6.opExtrude","SWEPT_BODY",BODY,{"disambiguationData":[OSD([sQuery(id+"F5.wireOp",EDGE,"E3.bottom"),sQuery(id+"F5.wireOp",EDGE,"E3.top"),sQuery(id+"F5.wireOp",EDGE,"E3.left"),sQuery(id+"F5.wireOp",EDGE,"E3.right")])]});
            var Q27;
            Q27=makeQuery(id+"F6.opExtrude","SWEPT_BODY",BODY,{"disambiguationData":[OSD([sQuery(id+"F5.wireOp",EDGE,"E1.bottom"),sQuery(id+"F5.wireOp",EDGE,"E1.top"),sQuery(id+"F5.wireOp",EDGE,"E1.left"),sQuery(id+"F5.wireOp",EDGE,"E1.right")])]});
            booleanBodies(context, id + "F34", {"operationType" : BooleanOperationType.SUBTRACTION, "tools" : qUnion([Q0, Q1, Q2, Q3, Q4, Q5, Q6, Q7, Q8, Q9, Q10, Q11, Q12, Q13, Q14, Q15, Q16, Q17, Q18, Q19, Q20, Q21, Q22, Q23]), "targets" : qUnion([Q24, Q25, Q26, Q27])});
        }
        {
            var Q0;
            Q0=qCreatedBy(makeId("Front.planeOp"),FACE);
            var sketch = newSketch(context, id + "F35", { "sketchPlane" : qUnion([Q0])});
            skLineSegment(sketch, "E36.bottom", {"start": v(-11, 117) * mm, "end": v(11, 117) * mm});
            skLineSegment(sketch, "E36.top", {"start": v(-11, 970) * mm, "end": v(11, 970) * mm});
            skLineSegment(sketch, "E36.left", {"start": v(-11, 117) * mm, "end": v(-11, 970) * mm});
            skLineSegment(sketch, "E36.right", {"start": v(11, 117) * mm, "end": v(11, 970) * mm});
            skPoint(sketch, "E36.middle", {"position": v(0, 543.5) * mm});
            skSolve(sketch);
        }
        {
            var Q0;
            Q0 = qSketchRegion(id + "F35", true);
            var Q1;
            Q1=makeQuery(id+"F14.opExtrude","SWEPT_FACE",FACE,{"disambiguationData":[OSD([sQuery(id+"F13.wireOp",EDGE,"E7.bottom")])]});
            var Q2;
            Q2=makeQuery(id+"F14.opExtrude","SWEPT_FACE",FACE,{"disambiguationData":[OSD([sQuery(id+"F13.wireOp",EDGE,"E7.top")])]});
            extrude(context, id + "F36", {"entities" : qUnion([Q0]), "endBound" : BoundingType.UP_TO_SURFACE, "oppositeDirection" : true, "endBoundEntityFace" : qUnion([Q1]), "depth" : 25 * mm, "hasSecondDirection" : true, "secondDirectionBound" : BoundingType.UP_TO_SURFACE, "secondDirectionOppositeDirection" : false, "secondDirectionBoundEntityFace" : qUnion([Q2]), "secondDirectionDepth" : 25 * mm});
        }
        {
            var Q0;
            Q0=makeQuery(id+"F4.opExtrude","CAP_FACE",FACE,{"disambiguationData":[OSD([sQuery(id+"F3.wireOp",EDGE,"E0.bottom"),sQuery(id+"F3.wireOp",EDGE,"E0.top"),sQuery(id+"F3.wireOp",EDGE,"E0.left"),sQuery(id+"F3.wireOp",EDGE,"E0.right")])],"isStart":true});
            var sketch = newSketch(context, id + "F37", { "sketchPlane" : qUnion([Q0])});
            skLineSegment(sketch, "E37.bottom", {"start": v(-600, 100) * mm, "end": v(-400, 100) * mm});
            skLineSegment(sketch, "E37.top", {"start": v(-600, -100) * mm, "end": v(-400, -100) * mm});
            skLineSegment(sketch, "E37.left", {"start": v(-600, 100) * mm, "end": v(-600, -100) * mm});
            skLineSegment(sketch, "E37.right", {"start": v(-400, 100) * mm, "end": v(-400, -100) * mm});
            skPoint(sketch, "E37.middle", {"position": v(-500, 0) * mm});
            skSolve(sketch);
        }
        {
            var Q0;
            Q0 = qSketchRegion(id + "F37", true);
            extrude(context, id + "F38", {"entities" : qUnion([Q0]), "operationType" : NewBodyOperationType.REMOVE, "endBound" : BoundingType.THROUGH_ALL, "oppositeDirection" : true, "depth" : 25 * mm});
        }
        {
            var Q0;
            Q0=makeQuery(id+"F4.opExtrude","CAP_FACE",FACE,{"disambiguationData":[OSD([sQuery(id+"F3.wireOp",EDGE,"E0.bottom"),sQuery(id+"F3.wireOp",EDGE,"E0.top"),sQuery(id+"F3.wireOp",EDGE,"E0.left"),sQuery(id+"F3.wireOp",EDGE,"E0.right")])],"isStart":true});
            var sketch = newSketch(context, id + "F39", { "sketchPlane" : qUnion([Q0])});
            skLineSegment(sketch, "E38.bottom", {"start": v(-610, 110) * mm, "end": v(-390, 110) * mm});
            skLineSegment(sketch, "E38.top", {"start": v(-610, -110) * mm, "end": v(-390, -110) * mm});
            skLineSegment(sketch, "E38.left", {"start": v(-610, 110) * mm, "end": v(-610, -110) * mm});
            skLineSegment(sketch, "E38.right", {"start": v(-390, 110) * mm, "end": v(-390, -110) * mm});
            skPoint(sketch, "E38.middle", {"position": v(-500, 0) * mm});
            skSolve(sketch);
        }
        {
            var Q0;
            Q0 = qSketchRegion(id + "F39", true);
            extrude(context, id + "F40", {"entities" : qUnion([Q0]), "operationType" : NewBodyOperationType.REMOVE, "oppositeDirection" : true, "depth" : 11 * mm});
        }
        {
            var Q0;
            Q0=makeQuery(id+"F40.boolean.opBoolean","COPY",FACE,{"derivedFrom":makeQuery(id+"F40.opExtrude","CAP_FACE",FACE,{"disambiguationData":[OSD([sQuery(id+"F39.wireOp",EDGE,"E38.bottom"),sQuery(id+"F39.wireOp",EDGE,"E38.top"),sQuery(id+"F39.wireOp",EDGE,"E38.left"),sQuery(id+"F39.wireOp",EDGE,"E38.right")])],"isStart":false})});
            var sketch = newSketch(context, id + "F41", { "sketchPlane" : qUnion([Q0])});
            skLineSegment(sketch, "E39.0", {"start": v(-400, -100) * mm, "end": v(-600, -100) * mm});
            skLineSegment(sketch, "E40.0", {"start": v(-400, -100) * mm, "end": v(-400, 100) * mm});
            skLineSegment(sketch, "E41.0", {"start": v(-400, 100) * mm, "end": v(-600, 100) * mm});
            skLineSegment(sketch, "E42.0", {"start": v(-600, -100) * mm, "end": v(-600, 100) * mm});
            skSolve(sketch);
        }
        {
            var Q0;
            Q0 = qSketchRegion(id + "F41", true);
            extrude(context, id + "F42", {"entities" : qUnion([Q0]), "oppositeDirection" : true, "depth" : 300 * mm});
        }
        {
            var Q0;
            Q0=makeQuery(id+"F42.opExtrude","CAP_FACE",FACE,{"disambiguationData":[OSD([sQuery(id+"F41.wireOp",EDGE,"E39.0"),sQuery(id+"F41.wireOp",EDGE,"E40.0"),sQuery(id+"F41.wireOp",EDGE,"E41.0"),sQuery(id+"F41.wireOp",EDGE,"E42.0")])],"isStart":true});
            shell(context, id + "F43", {"entities" : qUnion([Q0]), "thickness" : 1 * mm});
        }
        {
            var Q0;
            Q0=makeQuery(id+"F40.boolean.opBoolean","COPY",FACE,{"derivedFrom":makeQuery(id+"F40.opExtrude","CAP_FACE",FACE,{"disambiguationData":[OSD([sQuery(id+"F39.wireOp",EDGE,"E38.bottom"),sQuery(id+"F39.wireOp",EDGE,"E38.top"),sQuery(id+"F39.wireOp",EDGE,"E38.left"),sQuery(id+"F39.wireOp",EDGE,"E38.right")])],"isStart":false})});
            var sketch = newSketch(context, id + "F44", { "sketchPlane" : qUnion([Q0])});
            skLineSegment(sketch, "E43.0", {"start": v(-401, -99) * mm, "end": v(-401, 99) * mm});
            skLineSegment(sketch, "E44.0", {"start": v(-401, -99) * mm, "end": v(-599, -99) * mm});
            skLineSegment(sketch, "E45.0", {"start": v(-599, -99) * mm, "end": v(-599, 99) * mm});
            skLineSegment(sketch, "E46.0", {"start": v(-401, 99) * mm, "end": v(-599, 99) * mm});
            skLineSegment(sketch, "E47.bottom", {"start": v(-609, 109) * mm, "end": v(-391, 109) * mm});
            skLineSegment(sketch, "E47.top", {"start": v(-609, -109) * mm, "end": v(-391, -109) * mm});
            skLineSegment(sketch, "E47.left", {"start": v(-609, 109) * mm, "end": v(-609, -109) * mm});
            skLineSegment(sketch, "E47.right", {"start": v(-391, 109) * mm, "end": v(-391, -109) * mm});
            skPoint(sketch, "E47.middle", {"position": v(-500, 0) * mm});
            skSolve(sketch);
        }
        {
            var Q0;
            Q0 = qSketchRegion(id + "F44", true);
            extrude(context, id + "F45", {"entities" : qUnion([Q0]), "operationType" : NewBodyOperationType.ADD, "depth" : 1 * mm});
        }
        {
            var Q0;
            Q0=makeQuery(id+"F45.opExtrude","CAP_FACE",FACE,{"disambiguationData":[OSD([sQuery(id+"F44.wireOp",EDGE,"E43.0"),sQuery(id+"F44.wireOp",EDGE,"E44.0"),sQuery(id+"F44.wireOp",EDGE,"E45.0"),sQuery(id+"F44.wireOp",EDGE,"E46.0"),sQuery(id+"F44.wireOp",EDGE,"E47.bottom"),sQuery(id+"F44.wireOp",EDGE,"E47.top"),sQuery(id+"F44.wireOp",EDGE,"E47.left"),sQuery(id+"F44.wireOp",EDGE,"E47.right")])],"isStart":false});
            var sketch = newSketch(context, id + "F46", { "sketchPlane" : qUnion([Q0])});
            skLineSegment(sketch, "E48.bottom", {"start": v(-596, 96) * mm, "end": v(-404, 96) * mm});
            skLineSegment(sketch, "E48.top", {"start": v(-596, -96) * mm, "end": v(-404, -96) * mm});
            skLineSegment(sketch, "E48.left", {"start": v(-596, 96) * mm, "end": v(-596, -96) * mm});
            skLineSegment(sketch, "E48.right", {"start": v(-404, 96) * mm, "end": v(-404, -96) * mm});
            skPoint(sketch, "E48.middle", {"position": v(-500, 0) * mm});
            skSolve(sketch);
        }
        {
            var Q0;
            Q0 = qSketchRegion(id + "F46", true);
            extrude(context, id + "F47", {"entities" : qUnion([Q0]), "oppositeDirection" : true, "depth" : 10 * mm});
        }
        {
            var Q0;
            Q0=makeQuery(id+"F47.opExtrude","CAP_FACE",FACE,{"disambiguationData":[OSD([sQuery(id+"F46.wireOp",EDGE,"E48.bottom"),sQuery(id+"F46.wireOp",EDGE,"E48.top"),sQuery(id+"F46.wireOp",EDGE,"E48.left"),sQuery(id+"F46.wireOp",EDGE,"E48.right")])],"isStart":true});
            var sketch = newSketch(context, id + "F48", { "sketchPlane" : qUnion([Q0])});
            skLineSegment(sketch, "E49.bottom", {"start": v(-608, 108.5) * mm, "end": v(-391, 108.5) * mm});
            skLineSegment(sketch, "E49.top", {"start": v(-608, -108.5) * mm, "end": v(-391, -108.5) * mm});
            skLineSegment(sketch, "E49.left", {"start": v(-608, 108.5) * mm, "end": v(-608, -108.5) * mm});
            skLineSegment(sketch, "E49.right", {"start": v(-391, 108.5) * mm, "end": v(-391, -108.5) * mm});
            skPoint(sketch, "E49.middle", {"position": v(-499.5, 0) * mm});
            skSolve(sketch);
        }
        {
            var Q0;
            Q0 = qSketchRegion(id + "F48", true);
            extrude(context, id + "F49", {"entities" : qUnion([Q0]), "operationType" : NewBodyOperationType.ADD, "depth" : 10 * mm});
        }
    });
